# Revit family: РДК-50
name_source: partatom
category: Арматура трубопроводов
units: mm (PartAtom-declared; Revit-internal decimal feet)

## family parameters
Всегда вертикально = Да
На основе рабочей плоскости = Нет
Общий = Нет
При загрузке вырезать с полостями = Нет
Размер круглого соединителя = Использовать диаметр
Тип детали = Клапан - Вставляется

## types (7) — shared parameters
ADSK_Единица измерения = шт.
ADSK_Завод-изготовитель = РУП "БЕЛГАЗТЕХНИКА"
ADSK_Количество = 1
ADSK_Марка = РДК-50
ADSK_Масса_Текст = 22,0 кг
ADSK_Тип соединения = фланцевый
zero-valued in all types: Отметка по умолчанию

## per-type parameters (varying)
| type | ADSK_Диапазон выходного давления, МПа | ADSK_Наименование |
| исполнение 00 (0,0016-0,02) | 0,0016-0,02 | Регулятор РДК-50-00 ТУ BY 100270876.143-2008 |
| исполнение 01 (0,002-0,004) | 0,002-0,004 | Регулятор РДК-50-01 ТУ BY 100270876.143-2008 |
| исполнение 02 (0,004-0,007) | 0,004-0,007 | Регулятор РДК-50-02 ТУ BY 100270876.143-2008 |
| исполнение 03 (0,007-0,01) | 0,007-0,01 | Регулятор РДК-50-03 ТУ BY 100270876.143-2008 |
| исполнение 04 (0,01-0,015) | 0,01-0,015 | Регулятор РДК-50-04 ТУ BY 100270876.143-2008 |
| исполнение 05 (0,015-0,02) | 0,015-0,02 | Регулятор РДК-50-05 ТУ BY 100270876.143-2008 |
| исполнение 06 (0,02-0,03) | 0,02-0,03 | Регулятор РДК-50-06 ТУ BY 100270876.143-2008 |
